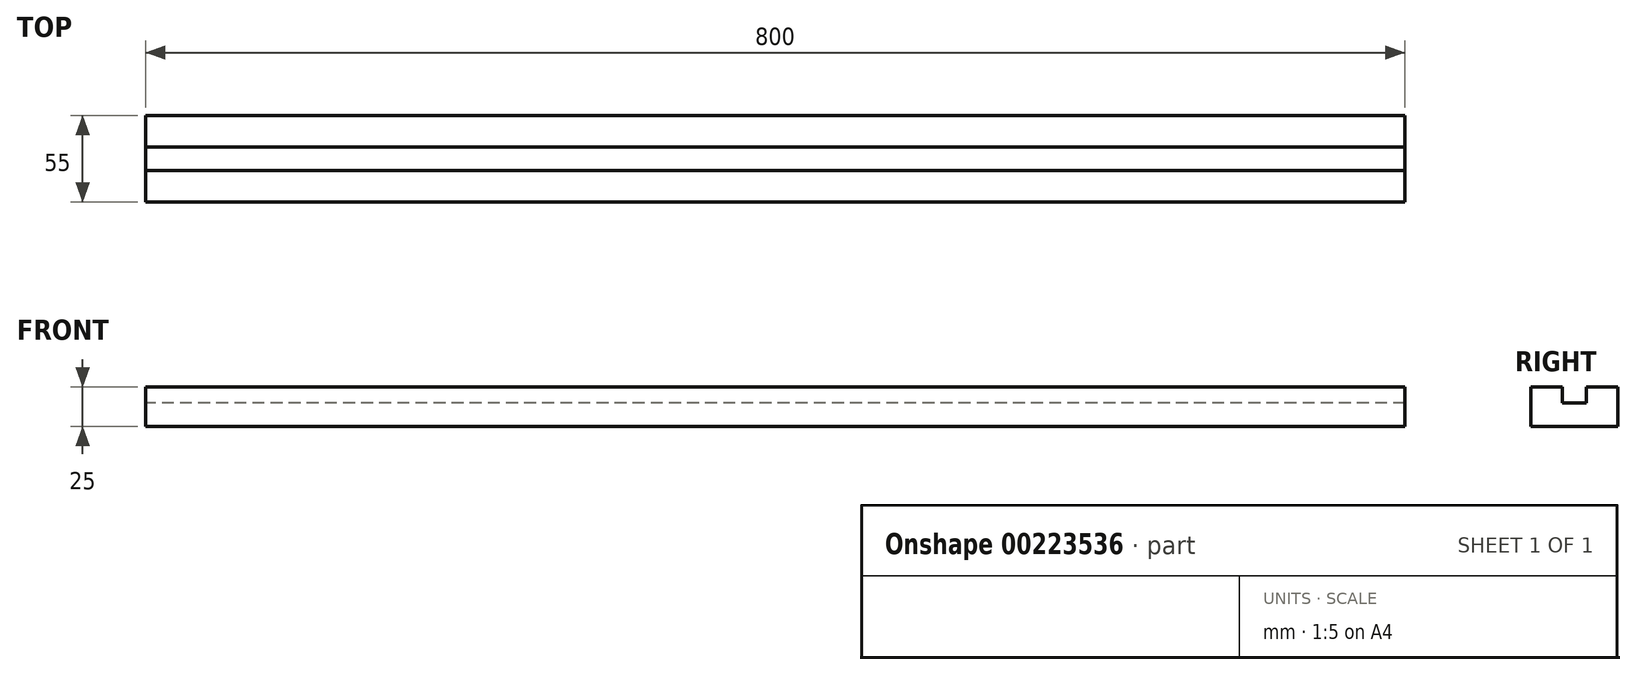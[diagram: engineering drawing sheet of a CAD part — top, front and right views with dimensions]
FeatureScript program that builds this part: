
annotation { "Feature Type Name" : "Feature", "Feature Type Description" : "" }
export const myFeature = defineFeature(function(context is Context, id is Id, definition is map)
    precondition{}
    {
        {
            var Q0;
            Q0=qCreatedBy(makeId("Right.planeOp"),FACE);
            var sketch = newSketch(context, id + "F0", { "sketchPlane" : qUnion([Q0])});
            skLineSegment(sketch, "E0", {"start": v(-7.5, 0) * mm, "end": v(7.5, 0) * mm});
            skLineSegment(sketch, "E1", {"start": v(-7.5, 0) * mm, "end": v(-7.5, 10) * mm});
            skLineSegment(sketch, "E2", {"start": v(-7.5, 10) * mm, "end": v(-27.5, 10) * mm});
            skLineSegment(sketch, "E3", {"start": v(-27.5, 10) * mm, "end": v(-27.5, -15) * mm});
            skLineSegment(sketch, "E4", {"start": v(0, 0) * mm, "end": v(0, 19.73) * mm, "construction": true});
            skLineSegment(sketch, "E5.MirrorCS", {"start": v(7.5, 0) * mm, "end": v(7.5, 10) * mm});
            skLineSegment(sketch, "E6.MirrorCS", {"start": v(7.5, 10) * mm, "end": v(27.5, 10) * mm});
            skLineSegment(sketch, "E7.MirrorCS", {"start": v(27.5, 10) * mm, "end": v(27.5, -15) * mm});
            skLineSegment(sketch, "E8", {"start": v(-27.5, -15) * mm, "end": v(27.5, -15) * mm});
            skSolve(sketch);
        }
        {
            var Q0;
            Q0=qSketchRegion(id+"F0",true);
            extrude(context, id + "F1", {"entities" : qUnion([Q0]), "depth" : 800 * mm});
        }
    });
